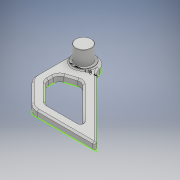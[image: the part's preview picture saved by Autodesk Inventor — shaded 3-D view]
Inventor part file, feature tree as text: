
AUTODESK INVENTOR PART (.ipt)
format: ipt  version: 2018.2 (Build 222227000, 227)  size: 188,416 bytes
history: native  units: mm
features: fillet x6, chamfer x4, extrude x3, sketch x2
ambient origin geometry x8: Origin, YZ Plane, XZ Plane, XY Plane, X Axis, Y Axis, Z Axis, Center Point
bodies: Solid1 (feature_tree)
feature tree (15):
  sketch  "Sketch1"  dims[d0=4.85mm d1=8.0mm]
  extrude  "Extrusion1"  Depth=8.0mm
  extrude  "Extrusion2"  Depth=3.0mm
  extrude  "Extrusion3"  Depth=2.0mm TaperAngle=0.0deg
  fillet  "Fillet1"  Radius=7.0mm
  fillet  "Fillet2"  Radius=0.75mm
  fillet  "Fillet3"  Radius=0.5mm
  fillet  "Fillet4"  Radius=2.0mm
  fillet  "Fillet5"  Radius=4.0mm
  fillet  "Fillet6"  Radius=4.0mm
  chamfer  "Chamfer1"  Distance=0.5mm
  chamfer  "Chamfer2"  Distance=0.5mm
  chamfer  "Chamfer3"  Distance=2.0mm
  chamfer  "Chamfer4"  Distance=2.0mm Angle=45.0deg
  sketch  "Sketch2"  dims[d4=3.0mm d5=3.0mm d6=2.0mm d7=0.0mm d8=7.0mm d9=0.0mm d10=0.75mm d11=0.5mm d12=0.0mm d13=2.0mm d14=4.0mm d15=4.0mm d16=0.5mm d17=0.5mm d18=2.0mm d19=0.1mm d20=2.0mm d21=45.0deg d22=0.5mm d23=2.0mm d24=45.0deg d25=0.3mm d26=2.0mm d27=45.0deg d28=0.5mm d29=2.0mm d30=45.0deg]
